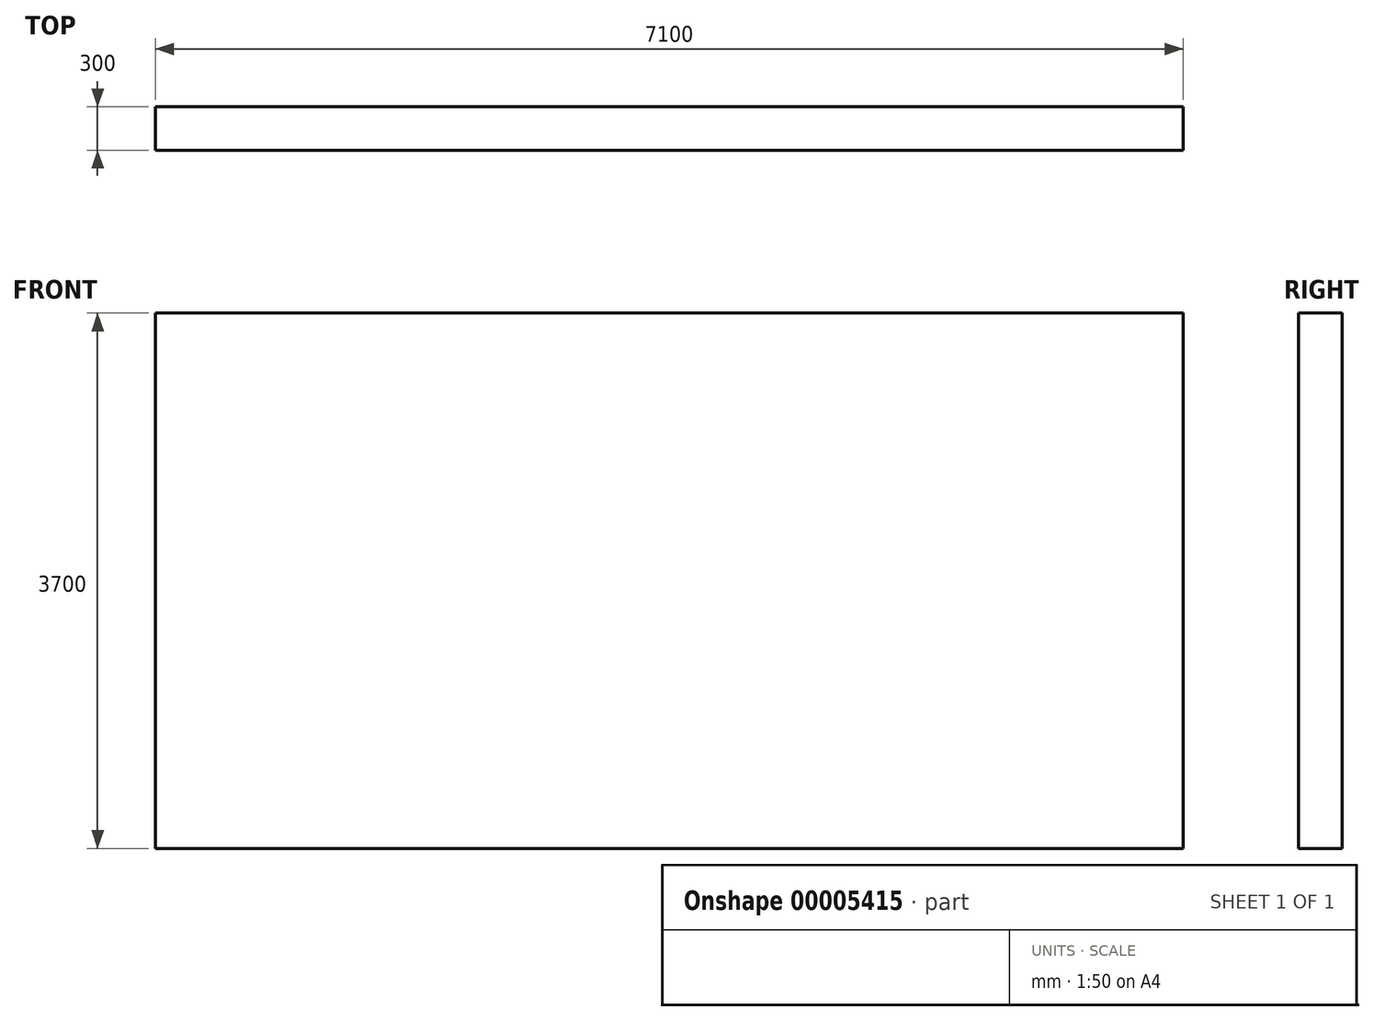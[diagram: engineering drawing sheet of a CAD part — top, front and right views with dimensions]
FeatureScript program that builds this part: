
annotation { "Feature Type Name" : "Feature", "Feature Type Description" : "" }
export const myFeature = defineFeature(function(context is Context, id is Id, definition is map)
    precondition{}
    {
        {
            var Q0;
            Q0=qCreatedBy(makeId("Front.planeOp"),FACE);
            var sketch = newSketch(context, id + "F0", { "sketchPlane" : qUnion([Q0])});
            skLineSegment(sketch, "E0.bottom", {"start": v(-3351.92, 1919.24) * mm, "end": v(3748.08, 1919.24) * mm});
            skLineSegment(sketch, "E0.top", {"start": v(-3351.92, -1780.76) * mm, "end": v(3748.08, -1780.76) * mm});
            skLineSegment(sketch, "E0.left", {"start": v(-3351.92, 1919.24) * mm, "end": v(-3351.92, -1780.76) * mm});
            skLineSegment(sketch, "E0.right", {"start": v(3748.08, 1919.24) * mm, "end": v(3748.08, -1780.76) * mm});
            skSolve(sketch);
        }
        {
            var Q0;
            Q0=qSketchRegion(id+"F0",true);
            extrude(context, id + "F1", {"entities" : qUnion([Q0]), "depth" : 300 * mm});
        }
    });
